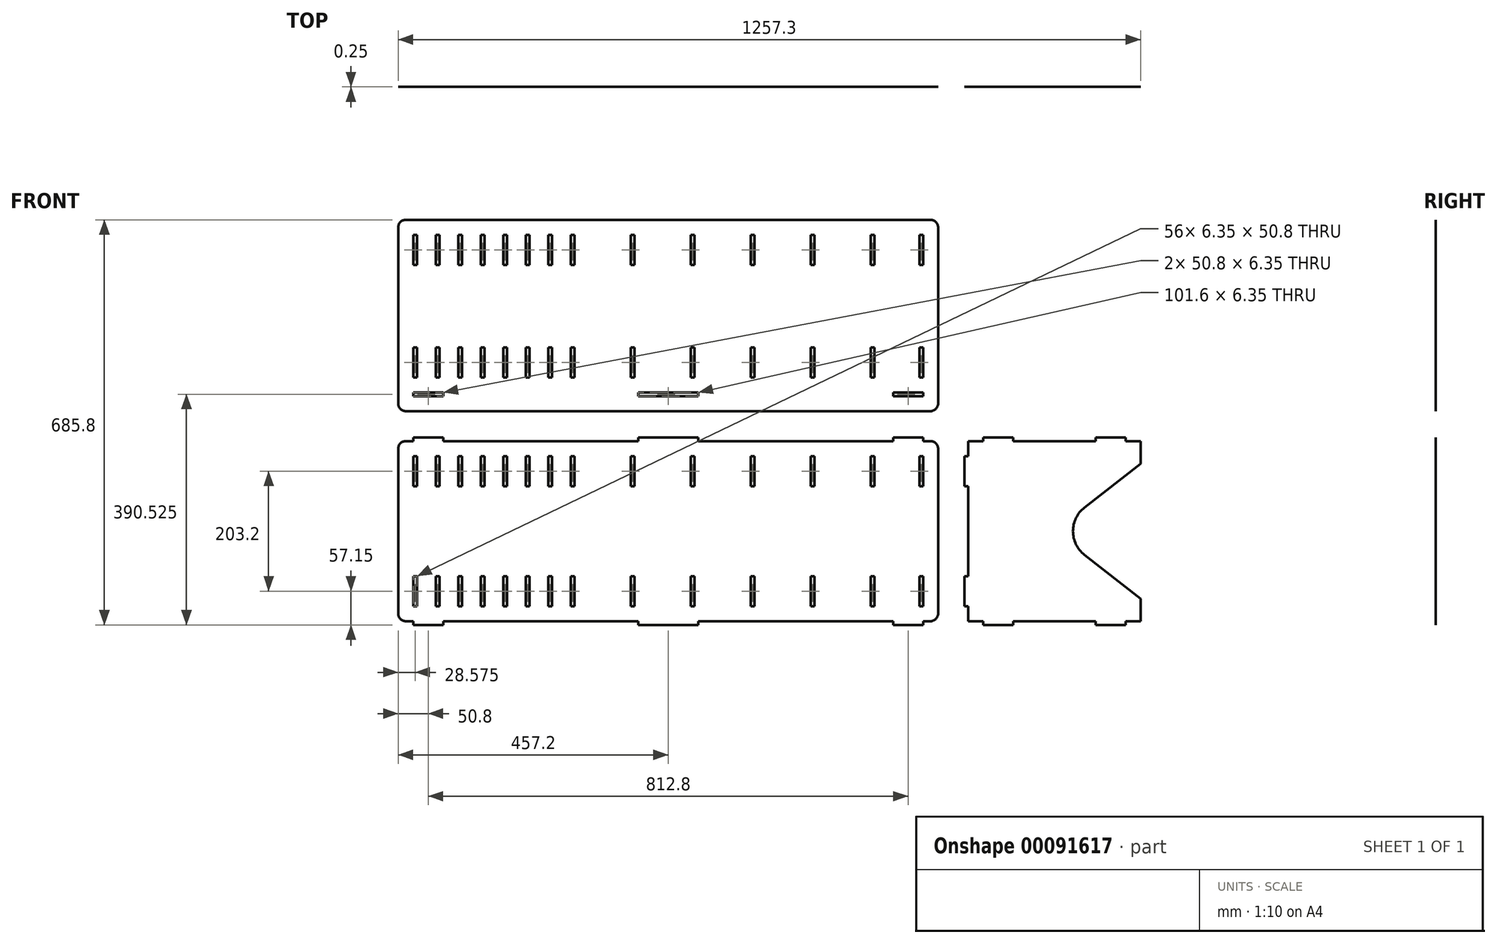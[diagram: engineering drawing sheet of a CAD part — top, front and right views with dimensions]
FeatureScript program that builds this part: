
annotation { "Feature Type Name" : "Feature", "Feature Type Description" : "" }
export const myFeature = defineFeature(function(context is Context, id is Id, definition is map)
    precondition{}
    {
        {
            assignVariable(context, id + "F0", {"name" : "Thickness", "anyValue" : .25});
        }
        {
            var Q0;
            Q0=qCreatedBy(makeId("Front.planeOp"),FACE);
            var sketch = newSketch(context, id + "F1", { "sketchPlane" : qUnion([Q0])});
            skLineSegment(sketch, "E0.bottom", {"start": v(-444.5, 152.4) * mm, "end": v(-431.8, 152.4) * mm});
            skLineSegment(sketch, "E0.top", {"start": v(-444.5, -152.4) * mm, "end": v(-431.8, -152.4) * mm});
            skLineSegment(sketch, "E0.left", {"start": v(-457.2, 139.7) * mm, "end": v(-457.2, -139.7) * mm});
            skLineSegment(sketch, "E0.right", {"start": v(457.2, 139.7) * mm, "end": v(457.2, -139.7) * mm});
            skPoint(sketch, "E0.middle", {"position": v(0, 0) * mm});
            skLineSegment(sketch, "E1.top", {"start": v(-431.8, 158.75) * mm, "end": v(-381, 158.75) * mm});
            skLineSegment(sketch, "E1.left", {"start": v(-431.8, 152.4) * mm, "end": v(-431.8, 158.75) * mm});
            skLineSegment(sketch, "E1.right", {"start": v(-381, 152.4) * mm, "end": v(-381, 158.75) * mm});
            skLineSegment(sketch, "E2.top", {"start": v(381, 158.75) * mm, "end": v(431.8, 158.75) * mm});
            skLineSegment(sketch, "E2.left", {"start": v(381, 152.4) * mm, "end": v(381, 158.75) * mm});
            skLineSegment(sketch, "E2.right", {"start": v(431.8, 152.4) * mm, "end": v(431.8, 158.75) * mm});
            skLineSegment(sketch, "E3.top", {"start": v(-50.8, 158.75) * mm, "end": v(50.8, 158.75) * mm});
            skLineSegment(sketch, "E3.left", {"start": v(-50.8, 152.4) * mm, "end": v(-50.8, 158.75) * mm});
            skLineSegment(sketch, "E3.right", {"start": v(50.8, 152.4) * mm, "end": v(50.8, 158.75) * mm});
            skLineSegment(sketch, "E4", {"start": v(-457.2, 0) * mm, "end": v(457.2, 0) * mm, "construction": true});
            skLineSegment(sketch, "E5.MirrorCS", {"start": v(431.8, -152.4) * mm, "end": v(431.8, -158.75) * mm});
            skLineSegment(sketch, "E6.MirrorCS", {"start": v(381, -152.4) * mm, "end": v(381, -158.75) * mm});
            skLineSegment(sketch, "E7.MirrorCS", {"start": v(-431.8, -152.4) * mm, "end": v(-431.8, -158.75) * mm});
            skLineSegment(sketch, "E8.MirrorCS", {"start": v(-381, -152.4) * mm, "end": v(-381, -158.75) * mm});
            skLineSegment(sketch, "E9.MirrorCS", {"start": v(50.8, -152.4) * mm, "end": v(50.8, -158.75) * mm});
            skLineSegment(sketch, "E10.MirrorCS", {"start": v(-50.8, -152.4) * mm, "end": v(-50.8, -158.75) * mm});
            skLineSegment(sketch, "E11.MirrorCS", {"start": v(381, -158.75) * mm, "end": v(431.8, -158.75) * mm});
            skLineSegment(sketch, "E12.MirrorCS", {"start": v(-50.8, -158.75) * mm, "end": v(50.8, -158.75) * mm});
            skLineSegment(sketch, "E13.MirrorCS", {"start": v(-431.8, -158.75) * mm, "end": v(-381, -158.75) * mm});
            skLineSegment(sketch, "E14.bottom", {"start": v(-444.5, 203.2) * mm, "end": v(444.5, 203.2) * mm});
            skLineSegment(sketch, "E14.top", {"start": v(-444.5, 527.05) * mm, "end": v(444.5, 527.05) * mm});
            skLineSegment(sketch, "E14.left", {"start": v(-457.2, 215.9) * mm, "end": v(-457.2, 514.35) * mm});
            skLineSegment(sketch, "E14.right", {"start": v(457.2, 215.9) * mm, "end": v(457.2, 514.35) * mm});
            skLineSegment(sketch, "E15", {"start": v(0, 158.75) * mm, "end": v(0, 228.6) * mm, "construction": true});
            skPoint(sketch, "E15.endSnap0", {"position": v(0, 203.2) * mm});
            skLineSegment(sketch, "E16", {"start": v(0, 193.67) * mm, "end": v(-50.8, 193.67) * mm, "construction": true});
            skPoint(sketch, "E16.endSnap0", {"position": v(0, 193.67) * mm});
            skLineSegment(sketch, "E17.MirrorCS", {"start": v(-50.8, 234.95) * mm, "end": v(-50.8, 228.6) * mm});
            skLineSegment(sketch, "E18.MirrorCS", {"start": v(50.8, 234.95) * mm, "end": v(50.8, 228.6) * mm});
            skLineSegment(sketch, "E19.MirrorCS", {"start": v(431.8, 234.95) * mm, "end": v(431.8, 228.6) * mm});
            skLineSegment(sketch, "E20.MirrorCS", {"start": v(381, 234.95) * mm, "end": v(381, 228.6) * mm});
            skLineSegment(sketch, "E21.MirrorCS", {"start": v(-381, 234.95) * mm, "end": v(-381, 228.6) * mm});
            skLineSegment(sketch, "E22.MirrorCS", {"start": v(-431.8, 234.95) * mm, "end": v(-431.8, 228.6) * mm});
            skLineSegment(sketch, "E23.MirrorCS", {"start": v(-50.8, 228.6) * mm, "end": v(50.8, 228.6) * mm});
            skLineSegment(sketch, "E24.MirrorCS", {"start": v(-50.8, 234.95) * mm, "end": v(50.8, 234.95) * mm});
            skLineSegment(sketch, "E25.MirrorCS", {"start": v(381, 228.6) * mm, "end": v(431.8, 228.6) * mm});
            skLineSegment(sketch, "E26.MirrorCS", {"start": v(381, 234.95) * mm, "end": v(431.8, 234.95) * mm});
            skLineSegment(sketch, "E27.MirrorCS", {"start": v(-431.8, 234.95) * mm, "end": v(-381, 234.95) * mm});
            skLineSegment(sketch, "E28.MirrorCS", {"start": v(-431.8, 228.6) * mm, "end": v(-381, 228.6) * mm});
            skLineSegment(sketch, "E29.bottom", {"start": v(431.8, 127) * mm, "end": v(425.45, 127) * mm});
            skLineSegment(sketch, "E29.top", {"start": v(431.8, 76.2) * mm, "end": v(425.45, 76.2) * mm});
            skLineSegment(sketch, "E29.left", {"start": v(431.8, 127) * mm, "end": v(431.8, 76.2) * mm});
            skLineSegment(sketch, "E29.right", {"start": v(425.45, 127) * mm, "end": v(425.45, 76.2) * mm});
            skLineSegment(sketch, "E30.MirrorCS", {"start": v(431.8, -127) * mm, "end": v(431.8, -76.2) * mm});
            skLineSegment(sketch, "E31.MirrorCS", {"start": v(431.8, -76.2) * mm, "end": v(425.45, -76.2) * mm});
            skLineSegment(sketch, "E32.MirrorCS", {"start": v(431.8, -127) * mm, "end": v(425.45, -127) * mm});
            skLineSegment(sketch, "E33.MirrorCS", {"start": v(425.45, -127) * mm, "end": v(425.45, -76.2) * mm});
            skLineSegment(sketch, "E34", {"start": v(0, 0) * mm, "end": v(0, -152.4) * mm, "construction": true});
            skLineSegment(sketch, "E35.MirrorCS", {"start": v(-431.8, -127) * mm, "end": v(-425.45, -127) * mm});
            skLineSegment(sketch, "E36.MirrorCS", {"start": v(-431.8, 76.2) * mm, "end": v(-425.45, 76.2) * mm});
            skLineSegment(sketch, "E37.MirrorCS", {"start": v(-431.8, -76.2) * mm, "end": v(-425.45, -76.2) * mm});
            skLineSegment(sketch, "E38.MirrorCS", {"start": v(-431.8, 127) * mm, "end": v(-425.45, 127) * mm});
            skLineSegment(sketch, "E39.MirrorCS", {"start": v(-431.8, 127) * mm, "end": v(-431.8, 76.2) * mm});
            skLineSegment(sketch, "E40.MirrorCS", {"start": v(-431.8, -127) * mm, "end": v(-431.8, -76.2) * mm});
            skLineSegment(sketch, "E41.MirrorCS", {"start": v(-425.45, -127) * mm, "end": v(-425.45, -76.2) * mm});
            skLineSegment(sketch, "E42.MirrorCS", {"start": v(-425.45, 127) * mm, "end": v(-425.45, 76.2) * mm});
            skLineSegment(sketch, "E43.bottom", {"start": v(431.8, 260.35) * mm, "end": v(425.45, 260.35) * mm});
            skLineSegment(sketch, "E43.top", {"start": v(431.8, 311.15) * mm, "end": v(425.45, 311.15) * mm});
            skLineSegment(sketch, "E43.left", {"start": v(431.8, 260.35) * mm, "end": v(431.8, 311.15) * mm});
            skLineSegment(sketch, "E43.right", {"start": v(425.45, 260.35) * mm, "end": v(425.45, 311.15) * mm});
            skLineSegment(sketch, "E44.MirrorCS", {"start": v(-431.8, 311.15) * mm, "end": v(-425.45, 311.15) * mm});
            skLineSegment(sketch, "E45.MirrorCS", {"start": v(-431.8, 260.35) * mm, "end": v(-425.45, 260.35) * mm});
            skLineSegment(sketch, "E46.MirrorCS", {"start": v(-431.8, 260.35) * mm, "end": v(-431.8, 311.15) * mm});
            skLineSegment(sketch, "E47.MirrorCS", {"start": v(-425.45, 260.35) * mm, "end": v(-425.45, 311.15) * mm});
            skLineSegment(sketch, "E48.bottom", {"start": v(508, 152.4) * mm, "end": v(533.4, 152.4) * mm});
            skLineSegment(sketch, "E48.top", {"start": v(508, -152.4) * mm, "end": v(533.4, -152.4) * mm});
            skLineSegment(sketch, "E48.left", {"start": v(508, 152.4) * mm, "end": v(508, 127) * mm});
            skLineSegment(sketch, "E48.right", {"start": v(800.1, 152.4) * mm, "end": v(800.1, 114.3) * mm});
            skLineSegment(sketch, "E49.bottom", {"start": v(508, 127) * mm, "end": v(501.65, 127) * mm});
            skLineSegment(sketch, "E49.top", {"start": v(508, 76.2) * mm, "end": v(501.65, 76.2) * mm});
            skLineSegment(sketch, "E49.right", {"start": v(501.65, 127) * mm, "end": v(501.65, 76.2) * mm});
            skLineSegment(sketch, "E50.bottom", {"start": v(508, -127) * mm, "end": v(501.65, -127) * mm});
            skLineSegment(sketch, "E50.top", {"start": v(508, -76.2) * mm, "end": v(501.65, -76.2) * mm});
            skLineSegment(sketch, "E50.left", {"start": v(508, -127) * mm, "end": v(508, -76.2) * mm});
            skLineSegment(sketch, "E50.right", {"start": v(501.65, -127) * mm, "end": v(501.65, -76.2) * mm});
            skLineSegment(sketch, "E51.top", {"start": v(533.4, 158.75) * mm, "end": v(584.2, 158.75) * mm});
            skLineSegment(sketch, "E51.left", {"start": v(533.4, 152.4) * mm, "end": v(533.4, 158.75) * mm});
            skLineSegment(sketch, "E51.right", {"start": v(584.2, 152.4) * mm, "end": v(584.2, 158.75) * mm});
            skLineSegment(sketch, "E52", {"start": v(654.05, 152.4) * mm, "end": v(654.05, -152.4) * mm, "construction": true});
            skLineSegment(sketch, "E53.MirrorCS", {"start": v(723.9, 152.4) * mm, "end": v(723.9, 158.75) * mm});
            skLineSegment(sketch, "E54.MirrorCS", {"start": v(774.7, 152.4) * mm, "end": v(774.7, 158.75) * mm});
            skLineSegment(sketch, "E55.MirrorCS", {"start": v(774.7, 158.75) * mm, "end": v(723.9, 158.75) * mm});
            skLineSegment(sketch, "E56.MirrorCS", {"start": v(723.9, -152.4) * mm, "end": v(723.9, -158.75) * mm});
            skLineSegment(sketch, "E57.MirrorCS", {"start": v(774.7, -152.4) * mm, "end": v(774.7, -158.75) * mm});
            skLineSegment(sketch, "E58.MirrorCS", {"start": v(533.4, -152.4) * mm, "end": v(533.4, -158.75) * mm});
            skLineSegment(sketch, "E59.MirrorCS", {"start": v(584.2, -152.4) * mm, "end": v(584.2, -158.75) * mm});
            skLineSegment(sketch, "E60.MirrorCS", {"start": v(533.4, -158.75) * mm, "end": v(584.2, -158.75) * mm});
            skLineSegment(sketch, "E61.MirrorCS", {"start": v(774.7, -158.75) * mm, "end": v(723.9, -158.75) * mm});
            skLineSegment(sketch, "E62", {"start": v(381, 234.95) * mm, "end": v(381, 527.05) * mm, "construction": true});
            skLineSegment(sketch, "E63", {"start": v(381, 381) * mm, "end": v(-457.2, 381) * mm, "construction": true});
            skLineSegment(sketch, "E64.MirrorCS", {"start": v(431.8, 450.85) * mm, "end": v(425.45, 450.85) * mm});
            skLineSegment(sketch, "E65.MirrorCS", {"start": v(431.8, 501.65) * mm, "end": v(425.45, 501.65) * mm});
            skLineSegment(sketch, "E66.MirrorCS", {"start": v(-431.8, 450.85) * mm, "end": v(-425.45, 450.85) * mm});
            skLineSegment(sketch, "E67.MirrorCS", {"start": v(-431.8, 501.65) * mm, "end": v(-425.45, 501.65) * mm});
            skLineSegment(sketch, "E68.MirrorCS", {"start": v(425.45, 501.65) * mm, "end": v(425.45, 450.85) * mm});
            skLineSegment(sketch, "E69.MirrorCS", {"start": v(-425.45, 501.65) * mm, "end": v(-425.45, 450.85) * mm});
            skLineSegment(sketch, "E70.MirrorCS", {"start": v(431.8, 501.65) * mm, "end": v(431.8, 450.85) * mm});
            skLineSegment(sketch, "E71.MirrorCS", {"start": v(-431.8, 501.65) * mm, "end": v(-431.8, 450.85) * mm});
            skLineSegment(sketch, "E72.1.0.0", {"start": v(-387.35, 127) * mm, "end": v(-387.35, 76.2) * mm});
            skLineSegment(sketch, "E72.1.0.1", {"start": v(-393.7, 127) * mm, "end": v(-393.7, 76.2) * mm});
            skLineSegment(sketch, "E72.1.0.2", {"start": v(-387.35, -127) * mm, "end": v(-387.35, -76.2) * mm});
            skLineSegment(sketch, "E72.1.0.3", {"start": v(-393.7, -127) * mm, "end": v(-393.7, -76.2) * mm});
            skLineSegment(sketch, "E72.1.0.5", {"start": v(-393.7, -127) * mm, "end": v(-387.35, -127) * mm});
            skLineSegment(sketch, "E72.1.0.6", {"start": v(-393.7, 127) * mm, "end": v(-387.35, 127) * mm});
            skLineSegment(sketch, "E72.1.0.7", {"start": v(-393.7, -76.2) * mm, "end": v(-387.35, -76.2) * mm});
            skLineSegment(sketch, "E72.1.0.8", {"start": v(-393.7, 76.2) * mm, "end": v(-387.35, 76.2) * mm});
            skLineSegment(sketch, "E72.2.0.0", {"start": v(-349.25, 127) * mm, "end": v(-349.25, 76.2) * mm});
            skLineSegment(sketch, "E72.2.0.1", {"start": v(-355.6, 127) * mm, "end": v(-355.6, 76.2) * mm});
            skLineSegment(sketch, "E72.2.0.2", {"start": v(-349.25, -127) * mm, "end": v(-349.25, -76.2) * mm});
            skLineSegment(sketch, "E72.2.0.3", {"start": v(-355.6, -127) * mm, "end": v(-355.6, -76.2) * mm});
            skLineSegment(sketch, "E72.2.0.5", {"start": v(-355.6, -127) * mm, "end": v(-349.25, -127) * mm});
            skLineSegment(sketch, "E72.2.0.6", {"start": v(-355.6, 127) * mm, "end": v(-349.25, 127) * mm});
            skLineSegment(sketch, "E72.2.0.7", {"start": v(-355.6, -76.2) * mm, "end": v(-349.25, -76.2) * mm});
            skLineSegment(sketch, "E72.2.0.8", {"start": v(-355.6, 76.2) * mm, "end": v(-349.25, 76.2) * mm});
            skLineSegment(sketch, "E72.3.0.0", {"start": v(-311.15, 127) * mm, "end": v(-311.15, 76.2) * mm});
            skLineSegment(sketch, "E72.3.0.1", {"start": v(-317.5, 127) * mm, "end": v(-317.5, 76.2) * mm});
            skLineSegment(sketch, "E72.3.0.2", {"start": v(-311.15, -127) * mm, "end": v(-311.15, -76.2) * mm});
            skLineSegment(sketch, "E72.3.0.3", {"start": v(-317.5, -127) * mm, "end": v(-317.5, -76.2) * mm});
            skLineSegment(sketch, "E72.3.0.5", {"start": v(-317.5, -127) * mm, "end": v(-311.15, -127) * mm});
            skLineSegment(sketch, "E72.3.0.6", {"start": v(-317.5, 127) * mm, "end": v(-311.15, 127) * mm});
            skLineSegment(sketch, "E72.3.0.7", {"start": v(-317.5, -76.2) * mm, "end": v(-311.15, -76.2) * mm});
            skLineSegment(sketch, "E72.3.0.8", {"start": v(-317.5, 76.2) * mm, "end": v(-311.15, 76.2) * mm});
            skLineSegment(sketch, "E72.4.0.0", {"start": v(-273.05, 127) * mm, "end": v(-273.05, 76.2) * mm});
            skLineSegment(sketch, "E72.4.0.1", {"start": v(-279.4, 127) * mm, "end": v(-279.4, 76.2) * mm});
            skLineSegment(sketch, "E72.4.0.2", {"start": v(-273.05, -127) * mm, "end": v(-273.05, -76.2) * mm});
            skLineSegment(sketch, "E72.4.0.3", {"start": v(-279.4, -127) * mm, "end": v(-279.4, -76.2) * mm});
            skLineSegment(sketch, "E72.4.0.5", {"start": v(-279.4, -127) * mm, "end": v(-273.05, -127) * mm});
            skLineSegment(sketch, "E72.4.0.6", {"start": v(-279.4, 127) * mm, "end": v(-273.05, 127) * mm});
            skLineSegment(sketch, "E72.4.0.7", {"start": v(-279.4, -76.2) * mm, "end": v(-273.05, -76.2) * mm});
            skLineSegment(sketch, "E72.4.0.8", {"start": v(-279.4, 76.2) * mm, "end": v(-273.05, 76.2) * mm});
            skLineSegment(sketch, "E72.5.0.0", {"start": v(-234.95, 127) * mm, "end": v(-234.95, 76.2) * mm});
            skLineSegment(sketch, "E72.5.0.1", {"start": v(-241.3, 127) * mm, "end": v(-241.3, 76.2) * mm});
            skLineSegment(sketch, "E72.5.0.2", {"start": v(-234.95, -127) * mm, "end": v(-234.95, -76.2) * mm});
            skLineSegment(sketch, "E72.5.0.3", {"start": v(-241.3, -127) * mm, "end": v(-241.3, -76.2) * mm});
            skLineSegment(sketch, "E72.5.0.5", {"start": v(-241.3, -127) * mm, "end": v(-234.95, -127) * mm});
            skLineSegment(sketch, "E72.5.0.6", {"start": v(-241.3, 127) * mm, "end": v(-234.95, 127) * mm});
            skLineSegment(sketch, "E72.5.0.7", {"start": v(-241.3, -76.2) * mm, "end": v(-234.95, -76.2) * mm});
            skLineSegment(sketch, "E72.5.0.8", {"start": v(-241.3, 76.2) * mm, "end": v(-234.95, 76.2) * mm});
            skLineSegment(sketch, "E72.6.0.0", {"start": v(-196.85, 127) * mm, "end": v(-196.85, 76.2) * mm});
            skLineSegment(sketch, "E72.6.0.1", {"start": v(-203.2, 127) * mm, "end": v(-203.2, 76.2) * mm});
            skLineSegment(sketch, "E72.6.0.2", {"start": v(-196.85, -127) * mm, "end": v(-196.85, -76.2) * mm});
            skLineSegment(sketch, "E72.6.0.3", {"start": v(-203.2, -127) * mm, "end": v(-203.2, -76.2) * mm});
            skLineSegment(sketch, "E72.6.0.5", {"start": v(-203.2, -127) * mm, "end": v(-196.85, -127) * mm});
            skLineSegment(sketch, "E72.6.0.6", {"start": v(-203.2, 127) * mm, "end": v(-196.85, 127) * mm});
            skLineSegment(sketch, "E72.6.0.7", {"start": v(-203.2, -76.2) * mm, "end": v(-196.85, -76.2) * mm});
            skLineSegment(sketch, "E72.6.0.8", {"start": v(-203.2, 76.2) * mm, "end": v(-196.85, 76.2) * mm});
            skLineSegment(sketch, "E72.7.0.0", {"start": v(-158.75, 127) * mm, "end": v(-158.75, 76.2) * mm});
            skLineSegment(sketch, "E72.7.0.1", {"start": v(-165.1, 127) * mm, "end": v(-165.1, 76.2) * mm});
            skLineSegment(sketch, "E72.7.0.2", {"start": v(-158.75, -127) * mm, "end": v(-158.75, -76.2) * mm});
            skLineSegment(sketch, "E72.7.0.3", {"start": v(-165.1, -127) * mm, "end": v(-165.1, -76.2) * mm});
            skLineSegment(sketch, "E72.7.0.5", {"start": v(-165.1, -127) * mm, "end": v(-158.75, -127) * mm});
            skLineSegment(sketch, "E72.7.0.6", {"start": v(-165.1, 127) * mm, "end": v(-158.75, 127) * mm});
            skLineSegment(sketch, "E72.7.0.7", {"start": v(-165.1, -76.2) * mm, "end": v(-158.75, -76.2) * mm});
            skLineSegment(sketch, "E72.7.0.8", {"start": v(-165.1, 76.2) * mm, "end": v(-158.75, 76.2) * mm});
            skLineSegment(sketch, "E72.direction1", {"start": v(-425.45, 76.2) * mm, "end": v(-387.35, 76.2) * mm, "construction": true});
            skLineSegment(sketch, "E73.1.0.0", {"start": v(-63.5, -127) * mm, "end": v(-63.5, -76.2) * mm});
            skLineSegment(sketch, "E73.1.0.1", {"start": v(-57.15, -127) * mm, "end": v(-57.15, -76.2) * mm});
            skLineSegment(sketch, "E73.1.0.2", {"start": v(-63.5, 127) * mm, "end": v(-63.5, 76.2) * mm});
            skLineSegment(sketch, "E73.1.0.3", {"start": v(-57.15, 127) * mm, "end": v(-57.15, 76.2) * mm});
            skLineSegment(sketch, "E73.1.0.4", {"start": v(-63.5, -76.2) * mm, "end": v(-57.15, -76.2) * mm});
            skLineSegment(sketch, "E73.1.0.5", {"start": v(-63.5, 76.2) * mm, "end": v(-57.15, 76.2) * mm});
            skLineSegment(sketch, "E73.1.0.6", {"start": v(-63.5, 127) * mm, "end": v(-57.15, 127) * mm});
            skLineSegment(sketch, "E73.1.0.7", {"start": v(-63.5, -127) * mm, "end": v(-57.15, -127) * mm});
            skLineSegment(sketch, "E73.2.0.0", {"start": v(38.1, -127) * mm, "end": v(38.1, -76.2) * mm});
            skLineSegment(sketch, "E73.2.0.1", {"start": v(44.45, -127) * mm, "end": v(44.45, -76.2) * mm});
            skLineSegment(sketch, "E73.2.0.2", {"start": v(38.1, 127) * mm, "end": v(38.1, 76.2) * mm});
            skLineSegment(sketch, "E73.2.0.3", {"start": v(44.45, 127) * mm, "end": v(44.45, 76.2) * mm});
            skLineSegment(sketch, "E73.2.0.4", {"start": v(38.1, -76.2) * mm, "end": v(44.45, -76.2) * mm});
            skLineSegment(sketch, "E73.2.0.5", {"start": v(38.1, 76.2) * mm, "end": v(44.45, 76.2) * mm});
            skLineSegment(sketch, "E73.2.0.6", {"start": v(38.1, 127) * mm, "end": v(44.45, 127) * mm});
            skLineSegment(sketch, "E73.2.0.7", {"start": v(38.1, -127) * mm, "end": v(44.45, -127) * mm});
            skLineSegment(sketch, "E73.3.0.0", {"start": v(139.7, -127) * mm, "end": v(139.7, -76.2) * mm});
            skLineSegment(sketch, "E73.3.0.1", {"start": v(146.05, -127) * mm, "end": v(146.05, -76.2) * mm});
            skLineSegment(sketch, "E73.3.0.2", {"start": v(139.7, 127) * mm, "end": v(139.7, 76.2) * mm});
            skLineSegment(sketch, "E73.3.0.3", {"start": v(146.05, 127) * mm, "end": v(146.05, 76.2) * mm});
            skLineSegment(sketch, "E73.3.0.4", {"start": v(139.7, -76.2) * mm, "end": v(146.05, -76.2) * mm});
            skLineSegment(sketch, "E73.3.0.5", {"start": v(139.7, 76.2) * mm, "end": v(146.05, 76.2) * mm});
            skLineSegment(sketch, "E73.3.0.6", {"start": v(139.7, 127) * mm, "end": v(146.05, 127) * mm});
            skLineSegment(sketch, "E73.3.0.7", {"start": v(139.7, -127) * mm, "end": v(146.05, -127) * mm});
            skLineSegment(sketch, "E73.4.0.0", {"start": v(241.3, -127) * mm, "end": v(241.3, -76.2) * mm});
            skLineSegment(sketch, "E73.4.0.1", {"start": v(247.65, -127) * mm, "end": v(247.65, -76.2) * mm});
            skLineSegment(sketch, "E73.4.0.2", {"start": v(241.3, 127) * mm, "end": v(241.3, 76.2) * mm});
            skLineSegment(sketch, "E73.4.0.3", {"start": v(247.65, 127) * mm, "end": v(247.65, 76.2) * mm});
            skLineSegment(sketch, "E73.4.0.4", {"start": v(241.3, -76.2) * mm, "end": v(247.65, -76.2) * mm});
            skLineSegment(sketch, "E73.4.0.5", {"start": v(241.3, 76.2) * mm, "end": v(247.65, 76.2) * mm});
            skLineSegment(sketch, "E73.4.0.6", {"start": v(241.3, 127) * mm, "end": v(247.65, 127) * mm});
            skLineSegment(sketch, "E73.4.0.7", {"start": v(241.3, -127) * mm, "end": v(247.65, -127) * mm});
            skLineSegment(sketch, "E73.5.0.0", {"start": v(342.9, -127) * mm, "end": v(342.9, -76.2) * mm});
            skLineSegment(sketch, "E73.5.0.1", {"start": v(349.25, -127) * mm, "end": v(349.25, -76.2) * mm});
            skLineSegment(sketch, "E73.5.0.2", {"start": v(342.9, 127) * mm, "end": v(342.9, 76.2) * mm});
            skLineSegment(sketch, "E73.5.0.3", {"start": v(349.25, 127) * mm, "end": v(349.25, 76.2) * mm});
            skLineSegment(sketch, "E73.5.0.4", {"start": v(342.9, -76.2) * mm, "end": v(349.25, -76.2) * mm});
            skLineSegment(sketch, "E73.5.0.5", {"start": v(342.9, 76.2) * mm, "end": v(349.25, 76.2) * mm});
            skLineSegment(sketch, "E73.5.0.6", {"start": v(342.9, 127) * mm, "end": v(349.25, 127) * mm});
            skLineSegment(sketch, "E73.5.0.7", {"start": v(342.9, -127) * mm, "end": v(349.25, -127) * mm});
            skLineSegment(sketch, "E73.direction1", {"start": v(-165.1, -127) * mm, "end": v(-63.5, -127) * mm, "construction": true});
            skLineSegment(sketch, "E74.1.0.0", {"start": v(-387.35, 501.65) * mm, "end": v(-387.35, 450.85) * mm});
            skLineSegment(sketch, "E74.1.0.1", {"start": v(-387.35, 260.35) * mm, "end": v(-387.35, 311.15) * mm});
            skLineSegment(sketch, "E74.1.0.2", {"start": v(-393.7, 260.35) * mm, "end": v(-393.7, 311.15) * mm});
            skLineSegment(sketch, "E74.1.0.3", {"start": v(-393.7, 501.65) * mm, "end": v(-393.7, 450.85) * mm});
            skLineSegment(sketch, "E74.1.0.4", {"start": v(-393.7, 311.15) * mm, "end": v(-387.35, 311.15) * mm});
            skLineSegment(sketch, "E74.1.0.5", {"start": v(-393.7, 260.35) * mm, "end": v(-387.35, 260.35) * mm});
            skLineSegment(sketch, "E74.1.0.6", {"start": v(-393.7, 501.65) * mm, "end": v(-387.35, 501.65) * mm});
            skLineSegment(sketch, "E74.1.0.7", {"start": v(-393.7, 450.85) * mm, "end": v(-387.35, 450.85) * mm});
            skLineSegment(sketch, "E74.2.0.0", {"start": v(-349.25, 501.65) * mm, "end": v(-349.25, 450.85) * mm});
            skLineSegment(sketch, "E74.2.0.1", {"start": v(-349.25, 260.35) * mm, "end": v(-349.25, 311.15) * mm});
            skLineSegment(sketch, "E74.2.0.2", {"start": v(-355.6, 260.35) * mm, "end": v(-355.6, 311.15) * mm});
            skLineSegment(sketch, "E74.2.0.3", {"start": v(-355.6, 501.65) * mm, "end": v(-355.6, 450.85) * mm});
            skLineSegment(sketch, "E74.2.0.4", {"start": v(-355.6, 311.15) * mm, "end": v(-349.25, 311.15) * mm});
            skLineSegment(sketch, "E74.2.0.5", {"start": v(-355.6, 260.35) * mm, "end": v(-349.25, 260.35) * mm});
            skLineSegment(sketch, "E74.2.0.6", {"start": v(-355.6, 501.65) * mm, "end": v(-349.25, 501.65) * mm});
            skLineSegment(sketch, "E74.2.0.7", {"start": v(-355.6, 450.85) * mm, "end": v(-349.25, 450.85) * mm});
            skLineSegment(sketch, "E74.3.0.0", {"start": v(-311.15, 501.65) * mm, "end": v(-311.15, 450.85) * mm});
            skLineSegment(sketch, "E74.3.0.1", {"start": v(-311.15, 260.35) * mm, "end": v(-311.15, 311.15) * mm});
            skLineSegment(sketch, "E74.3.0.2", {"start": v(-317.5, 260.35) * mm, "end": v(-317.5, 311.15) * mm});
            skLineSegment(sketch, "E74.3.0.3", {"start": v(-317.5, 501.65) * mm, "end": v(-317.5, 450.85) * mm});
            skLineSegment(sketch, "E74.3.0.4", {"start": v(-317.5, 311.15) * mm, "end": v(-311.15, 311.15) * mm});
            skLineSegment(sketch, "E74.3.0.5", {"start": v(-317.5, 260.35) * mm, "end": v(-311.15, 260.35) * mm});
            skLineSegment(sketch, "E74.3.0.6", {"start": v(-317.5, 501.65) * mm, "end": v(-311.15, 501.65) * mm});
            skLineSegment(sketch, "E74.3.0.7", {"start": v(-317.5, 450.85) * mm, "end": v(-311.15, 450.85) * mm});
            skLineSegment(sketch, "E74.4.0.0", {"start": v(-273.05, 501.65) * mm, "end": v(-273.05, 450.85) * mm});
            skLineSegment(sketch, "E74.4.0.1", {"start": v(-273.05, 260.35) * mm, "end": v(-273.05, 311.15) * mm});
            skLineSegment(sketch, "E74.4.0.2", {"start": v(-279.4, 260.35) * mm, "end": v(-279.4, 311.15) * mm});
            skLineSegment(sketch, "E74.4.0.3", {"start": v(-279.4, 501.65) * mm, "end": v(-279.4, 450.85) * mm});
            skLineSegment(sketch, "E74.4.0.4", {"start": v(-279.4, 311.15) * mm, "end": v(-273.05, 311.15) * mm});
            skLineSegment(sketch, "E74.4.0.5", {"start": v(-279.4, 260.35) * mm, "end": v(-273.05, 260.35) * mm});
            skLineSegment(sketch, "E74.4.0.6", {"start": v(-279.4, 501.65) * mm, "end": v(-273.05, 501.65) * mm});
            skLineSegment(sketch, "E74.4.0.7", {"start": v(-279.4, 450.85) * mm, "end": v(-273.05, 450.85) * mm});
            skLineSegment(sketch, "E74.5.0.0", {"start": v(-234.95, 501.65) * mm, "end": v(-234.95, 450.85) * mm});
            skLineSegment(sketch, "E74.5.0.1", {"start": v(-234.95, 260.35) * mm, "end": v(-234.95, 311.15) * mm});
            skLineSegment(sketch, "E74.5.0.2", {"start": v(-241.3, 260.35) * mm, "end": v(-241.3, 311.15) * mm});
            skLineSegment(sketch, "E74.5.0.3", {"start": v(-241.3, 501.65) * mm, "end": v(-241.3, 450.85) * mm});
            skLineSegment(sketch, "E74.5.0.4", {"start": v(-241.3, 311.15) * mm, "end": v(-234.95, 311.15) * mm});
            skLineSegment(sketch, "E74.5.0.5", {"start": v(-241.3, 260.35) * mm, "end": v(-234.95, 260.35) * mm});
            skLineSegment(sketch, "E74.5.0.6", {"start": v(-241.3, 501.65) * mm, "end": v(-234.95, 501.65) * mm});
            skLineSegment(sketch, "E74.5.0.7", {"start": v(-241.3, 450.85) * mm, "end": v(-234.95, 450.85) * mm});
            skLineSegment(sketch, "E74.6.0.0", {"start": v(-196.85, 501.65) * mm, "end": v(-196.85, 450.85) * mm});
            skLineSegment(sketch, "E74.6.0.1", {"start": v(-196.85, 260.35) * mm, "end": v(-196.85, 311.15) * mm});
            skLineSegment(sketch, "E74.6.0.2", {"start": v(-203.2, 260.35) * mm, "end": v(-203.2, 311.15) * mm});
            skLineSegment(sketch, "E74.6.0.3", {"start": v(-203.2, 501.65) * mm, "end": v(-203.2, 450.85) * mm});
            skLineSegment(sketch, "E74.6.0.4", {"start": v(-203.2, 311.15) * mm, "end": v(-196.85, 311.15) * mm});
            skLineSegment(sketch, "E74.6.0.5", {"start": v(-203.2, 260.35) * mm, "end": v(-196.85, 260.35) * mm});
            skLineSegment(sketch, "E74.6.0.6", {"start": v(-203.2, 501.65) * mm, "end": v(-196.85, 501.65) * mm});
            skLineSegment(sketch, "E74.6.0.7", {"start": v(-203.2, 450.85) * mm, "end": v(-196.85, 450.85) * mm});
            skLineSegment(sketch, "E74.7.0.0", {"start": v(-158.75, 501.65) * mm, "end": v(-158.75, 450.85) * mm});
            skLineSegment(sketch, "E74.7.0.1", {"start": v(-158.75, 260.35) * mm, "end": v(-158.75, 311.15) * mm});
            skLineSegment(sketch, "E74.7.0.2", {"start": v(-165.1, 260.35) * mm, "end": v(-165.1, 311.15) * mm});
            skLineSegment(sketch, "E74.7.0.3", {"start": v(-165.1, 501.65) * mm, "end": v(-165.1, 450.85) * mm});
            skLineSegment(sketch, "E74.7.0.4", {"start": v(-165.1, 311.15) * mm, "end": v(-158.75, 311.15) * mm});
            skLineSegment(sketch, "E74.7.0.5", {"start": v(-165.1, 260.35) * mm, "end": v(-158.75, 260.35) * mm});
            skLineSegment(sketch, "E74.7.0.6", {"start": v(-165.1, 501.65) * mm, "end": v(-158.75, 501.65) * mm});
            skLineSegment(sketch, "E74.7.0.7", {"start": v(-165.1, 450.85) * mm, "end": v(-158.75, 450.85) * mm});
            skLineSegment(sketch, "E74.direction1", {"start": v(-425.45, 450.85) * mm, "end": v(-387.35, 450.85) * mm, "construction": true});
            skLineSegment(sketch, "E75.1.0.0", {"start": v(-63.5, 501.65) * mm, "end": v(-63.5, 450.85) * mm});
            skLineSegment(sketch, "E75.1.0.1", {"start": v(-57.15, 260.35) * mm, "end": v(-57.15, 311.15) * mm});
            skLineSegment(sketch, "E75.1.0.2", {"start": v(-63.5, 260.35) * mm, "end": v(-63.5, 311.15) * mm});
            skLineSegment(sketch, "E75.1.0.3", {"start": v(-57.15, 501.65) * mm, "end": v(-57.15, 450.85) * mm});
            skLineSegment(sketch, "E75.1.0.4", {"start": v(-63.5, 311.15) * mm, "end": v(-57.15, 311.15) * mm});
            skLineSegment(sketch, "E75.1.0.5", {"start": v(-63.5, 501.65) * mm, "end": v(-57.15, 501.65) * mm});
            skLineSegment(sketch, "E75.1.0.6", {"start": v(-63.5, 450.85) * mm, "end": v(-57.15, 450.85) * mm});
            skLineSegment(sketch, "E75.1.0.7", {"start": v(-63.5, 260.35) * mm, "end": v(-57.15, 260.35) * mm});
            skLineSegment(sketch, "E75.2.0.0", {"start": v(38.1, 501.65) * mm, "end": v(38.1, 450.85) * mm});
            skLineSegment(sketch, "E75.2.0.1", {"start": v(44.45, 260.35) * mm, "end": v(44.45, 311.15) * mm});
            skLineSegment(sketch, "E75.2.0.2", {"start": v(38.1, 260.35) * mm, "end": v(38.1, 311.15) * mm});
            skLineSegment(sketch, "E75.2.0.3", {"start": v(44.45, 501.65) * mm, "end": v(44.45, 450.85) * mm});
            skLineSegment(sketch, "E75.2.0.4", {"start": v(38.1, 311.15) * mm, "end": v(44.45, 311.15) * mm});
            skLineSegment(sketch, "E75.2.0.5", {"start": v(38.1, 501.65) * mm, "end": v(44.45, 501.65) * mm});
            skLineSegment(sketch, "E75.2.0.6", {"start": v(38.1, 450.85) * mm, "end": v(44.45, 450.85) * mm});
            skLineSegment(sketch, "E75.2.0.7", {"start": v(38.1, 260.35) * mm, "end": v(44.45, 260.35) * mm});
            skLineSegment(sketch, "E75.3.0.0", {"start": v(139.7, 501.65) * mm, "end": v(139.7, 450.85) * mm});
            skLineSegment(sketch, "E75.3.0.1", {"start": v(146.05, 260.35) * mm, "end": v(146.05, 311.15) * mm});
            skLineSegment(sketch, "E75.3.0.2", {"start": v(139.7, 260.35) * mm, "end": v(139.7, 311.15) * mm});
            skLineSegment(sketch, "E75.3.0.3", {"start": v(146.05, 501.65) * mm, "end": v(146.05, 450.85) * mm});
            skLineSegment(sketch, "E75.3.0.4", {"start": v(139.7, 311.15) * mm, "end": v(146.05, 311.15) * mm});
            skLineSegment(sketch, "E75.3.0.5", {"start": v(139.7, 501.65) * mm, "end": v(146.05, 501.65) * mm});
            skLineSegment(sketch, "E75.3.0.6", {"start": v(139.7, 450.85) * mm, "end": v(146.05, 450.85) * mm});
            skLineSegment(sketch, "E75.3.0.7", {"start": v(139.7, 260.35) * mm, "end": v(146.05, 260.35) * mm});
            skLineSegment(sketch, "E75.4.0.0", {"start": v(241.3, 501.65) * mm, "end": v(241.3, 450.85) * mm});
            skLineSegment(sketch, "E75.4.0.1", {"start": v(247.65, 260.35) * mm, "end": v(247.65, 311.15) * mm});
            skLineSegment(sketch, "E75.4.0.2", {"start": v(241.3, 260.35) * mm, "end": v(241.3, 311.15) * mm});
            skLineSegment(sketch, "E75.4.0.3", {"start": v(247.65, 501.65) * mm, "end": v(247.65, 450.85) * mm});
            skLineSegment(sketch, "E75.4.0.4", {"start": v(241.3, 311.15) * mm, "end": v(247.65, 311.15) * mm});
            skLineSegment(sketch, "E75.4.0.5", {"start": v(241.3, 501.65) * mm, "end": v(247.65, 501.65) * mm});
            skLineSegment(sketch, "E75.4.0.6", {"start": v(241.3, 450.85) * mm, "end": v(247.65, 450.85) * mm});
            skLineSegment(sketch, "E75.4.0.7", {"start": v(241.3, 260.35) * mm, "end": v(247.65, 260.35) * mm});
            skLineSegment(sketch, "E75.5.0.0", {"start": v(342.9, 501.65) * mm, "end": v(342.9, 450.85) * mm});
            skLineSegment(sketch, "E75.5.0.1", {"start": v(349.25, 260.35) * mm, "end": v(349.25, 311.15) * mm});
            skLineSegment(sketch, "E75.5.0.2", {"start": v(342.9, 260.35) * mm, "end": v(342.9, 311.15) * mm});
            skLineSegment(sketch, "E75.5.0.3", {"start": v(349.25, 501.65) * mm, "end": v(349.25, 450.85) * mm});
            skLineSegment(sketch, "E75.5.0.4", {"start": v(342.9, 311.15) * mm, "end": v(349.25, 311.15) * mm});
            skLineSegment(sketch, "E75.5.0.5", {"start": v(342.9, 501.65) * mm, "end": v(349.25, 501.65) * mm});
            skLineSegment(sketch, "E75.5.0.6", {"start": v(342.9, 450.85) * mm, "end": v(349.25, 450.85) * mm});
            skLineSegment(sketch, "E75.5.0.7", {"start": v(342.9, 260.35) * mm, "end": v(349.25, 260.35) * mm});
            skLineSegment(sketch, "E75.direction1", {"start": v(-165.1, 450.85) * mm, "end": v(-63.5, 450.85) * mm, "construction": true});
            skPoint(sketch, "E76.visualSharp", {"position": v(-457.2, 527.05) * mm});
            skArc(sketch, "E76.filletArc", {"start": v(-444.5, 527.05) * mm, "mid": v(-453.48, 523.33) * mm, "end": v(-457.2, 514.35) * mm});
            skPoint(sketch, "E77.visualSharp", {"position": v(457.2, 527.05) * mm});
            skArc(sketch, "E77.filletArc", {"start": v(457.2, 514.35) * mm, "mid": v(453.48, 523.33) * mm, "end": v(444.5, 527.05) * mm});
            skPoint(sketch, "E78.visualSharp", {"position": v(457.2, 203.2) * mm});
            skArc(sketch, "E78.filletArc", {"start": v(444.5, 203.2) * mm, "mid": v(453.48, 206.92) * mm, "end": v(457.2, 215.9) * mm});
            skPoint(sketch, "E79.visualSharp", {"position": v(-457.2, 203.2) * mm});
            skArc(sketch, "E79.filletArc", {"start": v(-457.2, 215.9) * mm, "mid": v(-453.48, 206.92) * mm, "end": v(-444.5, 203.2) * mm});
            skPoint(sketch, "E80.visualSharp", {"position": v(-457.2, 152.4) * mm});
            skArc(sketch, "E80.filletArc", {"start": v(-444.5, 152.4) * mm, "mid": v(-453.48, 148.68) * mm, "end": v(-457.2, 139.7) * mm});
            skPoint(sketch, "E81.visualSharp", {"position": v(457.2, 152.4) * mm});
            skArc(sketch, "E81.filletArc", {"start": v(457.2, 139.7) * mm, "mid": v(453.48, 148.68) * mm, "end": v(444.5, 152.4) * mm});
            skPoint(sketch, "E82.visualSharp", {"position": v(457.2, -152.4) * mm});
            skArc(sketch, "E82.filletArc", {"start": v(444.5, -152.4) * mm, "mid": v(453.48, -148.68) * mm, "end": v(457.2, -139.7) * mm});
            skPoint(sketch, "E83.visualSharp", {"position": v(-457.2, -152.4) * mm});
            skArc(sketch, "E83.filletArc", {"start": v(-457.2, -139.7) * mm, "mid": v(-453.48, -148.68) * mm, "end": v(-444.5, -152.4) * mm});
            skLineSegment(sketch, "E84", {"start": v(705.17, 40) * mm, "end": v(800.1, 114.3) * mm});
            skLineSegment(sketch, "E85", {"start": v(705.17, -40) * mm, "end": v(800.1, -114.3) * mm});
            skPoint(sketch, "E86.visualSharp", {"position": v(654.05, 0) * mm});
            skArc(sketch, "E86.filletArc", {"start": v(705.17, 40) * mm, "mid": v(685.68, 0) * mm, "end": v(705.17, -40) * mm});
            skLineSegment(sketch, "E87.trimOffspring", {"start": v(-381, 152.4) * mm, "end": v(-50.8, 152.4) * mm});
            skLineSegment(sketch, "E88.trimOffspring", {"start": v(50.8, 152.4) * mm, "end": v(381, 152.4) * mm});
            skLineSegment(sketch, "E89.trimOffspring", {"start": v(431.8, 152.4) * mm, "end": v(444.5, 152.4) * mm});
            skLineSegment(sketch, "E90.trimOffspring", {"start": v(584.2, 152.4) * mm, "end": v(723.9, 152.4) * mm});
            skLineSegment(sketch, "E91.trimOffspring", {"start": v(508, 76.2) * mm, "end": v(508, -152.4) * mm});
            skLineSegment(sketch, "E92.trimOffspring", {"start": v(774.7, 152.4) * mm, "end": v(800.1, 152.4) * mm});
            skLineSegment(sketch, "E93.trimOffspring", {"start": v(800.1, -114.3) * mm, "end": v(800.1, -152.4) * mm});
            skLineSegment(sketch, "E94.trimOffspring", {"start": v(431.8, -152.4) * mm, "end": v(444.5, -152.4) * mm});
            skLineSegment(sketch, "E95.trimOffspring", {"start": v(774.7, -152.4) * mm, "end": v(800.1, -152.4) * mm});
            skLineSegment(sketch, "E96.trimOffspring", {"start": v(584.2, -152.4) * mm, "end": v(723.9, -152.4) * mm});
            skLineSegment(sketch, "E97.trimOffspring", {"start": v(50.8, -152.4) * mm, "end": v(381, -152.4) * mm});
            skLineSegment(sketch, "E98.trimOffspring", {"start": v(-381, -152.4) * mm, "end": v(-50.8, -152.4) * mm});
            skSolve(sketch);
        }
        {
            var Q0;
            Q0=makeQuery(id+"F1.imprint","IMPRINT",FACE,{"disambiguationData":[TD([[makeQuery(id+"F1.imprint","IMPRINT",EDGE,{"derivedFrom":sQuery(id+"F1.wireOp",EDGE,"E14.bottom")}),1.0]])]});
            var Q1;
            {var subQ8=sQuery(id+"F1.wireOp",EDGE,"E0.left");Q1=makeQuery(id+"F1.imprint","IMPRINT",FACE,{"disambiguationData":[TD([[makeQuery(id+"F1.imprint","IMPRINT",EDGE,{"derivedFrom":subQ8}),1.0]])]});}
            var Q2;
            Q2=makeQuery(id+"F1.imprint","IMPRINT",FACE,{"disambiguationData":[TD([[makeQuery(id+"F1.imprint","IMPRINT",EDGE,{"derivedFrom":sQuery(id+"F1.wireOp",EDGE,"E1.bottom")}),1.0]])]});
            var Q3;
            Q3=makeQuery(id+"F1.imprint","IMPRINT",FACE,{"disambiguationData":[TD([[makeQuery(id+"F1.imprint","IMPRINT",EDGE,{"derivedFrom":sQuery(id+"F1.wireOp",EDGE,"E3.bottom")}),1.0]])]});
            var Q4;
            Q4=makeQuery(id+"F1.imprint","IMPRINT",FACE,{"disambiguationData":[TD([[makeQuery(id+"F1.imprint","IMPRINT",EDGE,{"derivedFrom":sQuery(id+"F1.wireOp",EDGE,"E2.bottom")}),1.0]])]});
            var Q5;
            Q5=makeQuery(id+"F1.imprint","IMPRINT",FACE,{"disambiguationData":[TD([[makeQuery(id+"F1.imprint","IMPRINT",EDGE,{"derivedFrom":sQuery(id+"F1.wireOp",EDGE,"E51.bottom")}),1.0]])]});
            var Q6;
            Q6=makeQuery(id+"F1.imprint","IMPRINT",FACE,{"disambiguationData":[TD([[makeQuery(id+"F1.imprint","IMPRINT",EDGE,{"derivedFrom":sQuery(id+"F1.wireOp",EDGE,"E53.MirrorCS")}),-1.0]])]});
            var Q7;
            Q7=makeQuery(id+"F1.imprint","IMPRINT",FACE,{"disambiguationData":[TD([[makeQuery(id+"F1.imprint","IMPRINT",EDGE,{"derivedFrom":sQuery(id+"F1.wireOp",EDGE,"E49.bottom")}),1.0]])]});
            var Q8;
            Q8=makeQuery(id+"F1.imprint","IMPRINT",FACE,{"disambiguationData":[TD([[makeQuery(id+"F1.imprint","IMPRINT",EDGE,{"derivedFrom":sQuery(id+"F1.wireOp",EDGE,"E50.bottom")}),-1.0]])]});
            var Q9;
            {var subQ4=sQuery(id+"F1.wireOp",EDGE,"E48.top");Q9=makeQuery(id+"F1.imprint","IMPRINT",FACE,{"disambiguationData":[TD([[makeQuery(id+"F1.imprint","IMPRINT",EDGE,{"derivedFrom":subQ4}),1.0]])]});}
            var Q10;
            Q10=makeQuery(id+"F1.imprint","IMPRINT",FACE,{"disambiguationData":[TD([[makeQuery(id+"F1.imprint","IMPRINT",EDGE,{"derivedFrom":sQuery(id+"F1.wireOp",EDGE,"E5.MirrorCS")}),-1.0]])]});
            var Q11;
            Q11=makeQuery(id+"F1.imprint","IMPRINT",FACE,{"disambiguationData":[TD([[makeQuery(id+"F1.imprint","IMPRINT",EDGE,{"derivedFrom":sQuery(id+"F1.wireOp",EDGE,"E9.MirrorCS")}),-1.0]])]});
            var Q12;
            Q12=makeQuery(id+"F1.imprint","IMPRINT",FACE,{"disambiguationData":[TD([[makeQuery(id+"F1.imprint","IMPRINT",EDGE,{"derivedFrom":sQuery(id+"F1.wireOp",EDGE,"E7.MirrorCS")}),1.0]])]});
            var Q13;
            Q13=makeQuery(id+"F1.imprint","IMPRINT",FACE,{"disambiguationData":[TD([[makeQuery(id+"F1.imprint","IMPRINT",EDGE,{"derivedFrom":sQuery(id+"F1.wireOp",EDGE,"E56.MirrorCS")}),1.0]])]});
            var Q14;
            Q14=makeQuery(id+"F1.imprint","IMPRINT",FACE,{"disambiguationData":[TD([[makeQuery(id+"F1.imprint","IMPRINT",EDGE,{"derivedFrom":sQuery(id+"F1.wireOp",EDGE,"E58.MirrorCS")}),1.0]])]});
            extrude(context, id + "F2", {"entities" : qUnion([Q0, Q1, Q2, Q3, Q4, Q5, Q6, Q7, Q8, Q9, Q10, Q11, Q12, Q13, Q14]), "depth" : (getVariable(context, 'Thickness')) * mm});
        }
    });
